# Revit family: Table-Teknion-CQTAZ_Racetrack_Agile_Table-R2020
name_source: partatom
category: Furniture
units: mm (PartAtom-declared; Revit-internal decimal feet)

## family parameters
Always vertical = Yes
Cut with Voids When Loaded = No
OmniClass Number = 23.40.20.00
OmniClass Title = General Furniture and Specialties
Room Calculation Point = No
Shared = Yes
Work Plane-Based = No

## types (3) — shared parameters
Assembly Code = E2020200
Caster Finish = Plastic - Teknion - E - Ebony
Foot Finish = Plastic - Teknion - E - Ebony
Manufacturer = Teknion
Manufacturer Fax = 416.661.4586
Part Number = CQTAZ
Product Documentation Link = https://assets.teknion.com
Product Line = Routes Tables
Product Page URL = https://www.teknion.com
Series = Routes
Sustainability Data = https://www.teknion.com
URL = www.teknion.com
Unit Weight URL = http://www.teknion.com
Warranty = http://www.teknion.com
zero-valued in all types: Default Elevation

## per-type parameters (varying)
| type | Description | Height | Model | Support Frame | Support Surface |
| Task Height | Racetrack Agile Table, Task Height, 22" Depth, 72" Width | 29 " | CQTAZT2272 | No | Yes |
| Counter Height | Racetrack Agile Table, Counter Height, 22" Depth, 72" Width | 36 " | CQTAZC2272 | Yes | No |
| Bar Height | Racetrack Agile Table, Bar Height, 22" Depth, 72" Width | 42 " | CQTAZB2272 | Yes | No |

## geometry (parser evidence)
native form markers: Sweep x2
no freeform markers — native parametric forms only
